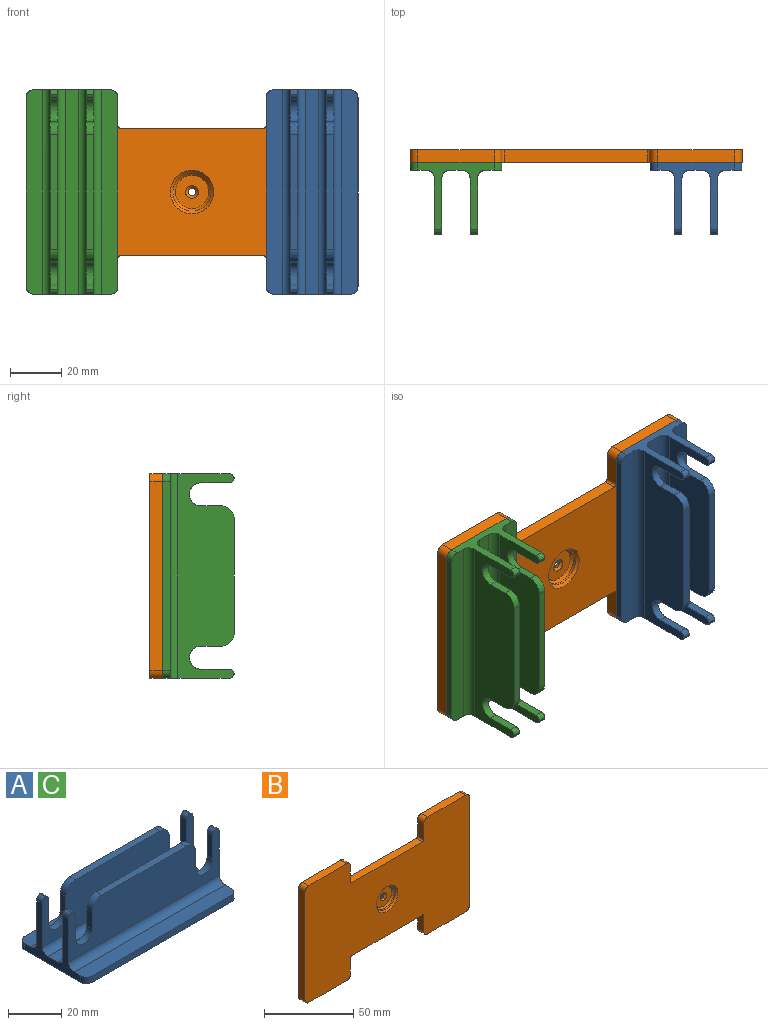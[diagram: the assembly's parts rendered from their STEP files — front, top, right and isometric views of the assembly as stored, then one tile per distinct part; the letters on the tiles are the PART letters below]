
ASSEMBLY  parts=3 mates=6
PART A: 151 faces, bbox 81.2x37.2x29.2 mm
  f0: plane 80x22mm, normal (0,1,0), area 1448.2mm2, adj f25,f26,f27,f116,f126,f128,f135,f136
  f1: plane 80x22mm, normal (0,-1,0), area 1448.2mm2, adj f25,f26,f27,f117,f126,f128,f135,f136
  f2: plane 81.23x23.23mm, normal (0,1,0), area 1448.2mm2, adj f124,f125,f126,f128,f129,f130,f131,f132
  f3: plane 80x22mm, normal (0,-1,0), area 1448.2mm2, adj f125,f126,f127,f128,f129,f130,f131,f132
  f4: plane 7.07x7.07mm, normal (0,0,-1), area 25mm2, adj f29,f30,f31,f32
  f5: plane 7.07x7.07mm, normal (0,0,-1), area 25mm2, adj f33,f34,f35,f36
  f6: plane 7.07x7.07mm, normal (0,0,-1), area 25mm2, adj f37,f38,f39,f40
  f7: plane 7.07x7.07mm, normal (0,0,-1), area 25mm2, adj f41,f42,f43,f44
  f8: plane 7.07x7.07mm, normal (0,0,-1), area 25mm2, adj f45,f46,f47,f48
  f9: plane 7.07x7.07mm, normal (0,0,-1), area 25mm2, adj f49,f50,f51,f52
  f10: plane 7.07x7.07mm, normal (0,0,-1), area 25mm2, adj f53,f54,f55,f56
  f11: plane 7.07x7.07mm, normal (0,0,-1), area 25mm2, adj f57,f58,f59,f60
  f12: plane 7.07x7.07mm, normal (0,0,-1), area 25mm2, adj f61,f62,f63,f64
  f13: plane 7.07x7.07mm, normal (0,0,-1), area 25mm2, adj f65,f66,f67,f68
  f14: plane 7.07x7.07mm, normal (0,0,-1), area 25mm2, adj f69,f70,f71,f72
  f15: plane 7.07x7.07mm, normal (0,0,-1), area 25mm2, adj f73,f74,f75,f76
  f16: plane 7.07x7.07mm, normal (0,0,-1), area 25mm2, adj f77,f78,f79,f80
  f17: plane 7.07x7.07mm, normal (0,0,-1), area 25mm2, adj f81,f82,f83,f84
  f18: plane 7.07x7.07mm, normal (0,0,-1), area 25mm2, adj f85,f86,f87,f88
  f19: plane 7.07x7.07mm, normal (0,0,-1), area 25mm2, adj f89,f90,f91,f92
  f20: plane 7.07x7.07mm, normal (0,0,-1), area 25mm2, adj f93,f94,f95,f96
  f21: plane 7.07x7.07mm, normal (0,0,-1), area 25mm2, adj f97,f98,f99,f100
  f22: plane 7.07x7.07mm, normal (0,0,-1), area 25mm2, adj f101,f102,f103,f104
  f23: plane 7.07x7.07mm, normal (0,0,-1), area 25mm2, adj f105,f106,f107,f108
  f24: plane 7.07x7.07mm, normal (0,0,-1), area 25mm2, adj f109,f110,f111,f112
  f25: plane 44.84x3mm, normal (0,0,1), area 134.5mm2, adj f0,f1,f141,f142
  f26: cylinder r=4.5mm len=9mm, axis (0,-1,0), area 42.4mm2, adj f0,f1,f135,f136
  f27: cylinder r=4.5mm len=9mm, axis (0,-1,0), area 42.4mm2, adj f0,f1,f137,f138
  f28: plane 74x3mm, normal (0,-1,0), area 222mm2, adj f114,f119,f120,f121
  f29: plane 3.54x3.54mm, normal (-0.71,-0.71,0), area 2.5mm2, adj f4,f30,f32,f121
  f30: plane 3.54x3.54mm, normal (0.71,-0.71,0), area 2.5mm2, adj f4,f29,f31,f121
  f31: plane 3.54x3.54mm, normal (0.71,0.71,0), area 2.5mm2, adj f4,f30,f32,f121
  f32: plane 3.54x3.54mm, normal (-0.71,0.71,0), area 2.5mm2, adj f4,f29,f31,f121
  f33: plane 3.54x3.54mm, normal (-0.71,-0.71,0), area 2.5mm2, adj f5,f34,f36,f121
  f34: plane 3.54x3.54mm, normal (0.71,-0.71,0), area 2.5mm2, adj f5,f33,f35,f121
  f35: plane 3.54x3.54mm, normal (0.71,0.71,0), area 2.5mm2, adj f5,f34,f36,f121
  f36: plane 3.54x3.54mm, normal (-0.71,0.71,0), area 2.5mm2, adj f5,f33,f35,f121
  f37: plane 3.54x3.54mm, normal (-0.71,-0.71,0), area 2.5mm2, adj f6,f38,f40,f121
  f38: plane 3.54x3.54mm, normal (0.71,-0.71,0), area 2.5mm2, adj f6,f37,f39,f121
  f39: plane 3.54x3.54mm, normal (0.71,0.71,0), area 2.5mm2, adj f6,f38,f40,f121
  f40: plane 3.54x3.54mm, normal (-0.71,0.71,0), area 2.5mm2, adj f6,f37,f39,f121
  f41: plane 3.54x3.54mm, normal (-0.71,-0.71,0), area 2.5mm2, adj f7,f42,f44,f121
  f42: plane 3.54x3.54mm, normal (0.71,-0.71,0), area 2.5mm2, adj f7,f41,f43,f121
  f43: plane 3.54x3.54mm, normal (0.71,0.71,0), area 2.5mm2, adj f7,f42,f44,f121
  f44: plane 3.54x3.54mm, normal (-0.71,0.71,0), area 2.5mm2, adj f7,f41,f43,f121
  f45: plane 3.54x3.54mm, normal (-0.71,-0.71,0), area 2.5mm2, adj f8,f46,f48,f121
  f46: plane 3.54x3.54mm, normal (0.71,-0.71,0), area 2.5mm2, adj f8,f45,f47,f121
  f47: plane 3.54x3.54mm, normal (0.71,0.71,0), area 2.5mm2, adj f8,f46,f48,f121
  f48: plane 3.54x3.54mm, normal (-0.71,0.71,0), area 2.5mm2, adj f8,f45,f47,f121
  f49: plane 3.54x3.54mm, normal (-0.71,-0.71,0), area 2.5mm2, adj f9,f50,f52,f121
  f50: plane 3.54x3.54mm, normal (0.71,-0.71,0), area 2.5mm2, adj f9,f49,f51,f121
  f51: plane 3.54x3.54mm, normal (0.71,0.71,0), area 2.5mm2, adj f9,f50,f52,f121
  f52: plane 3.54x3.54mm, normal (-0.71,0.71,0), area 2.5mm2, adj f9,f49,f51,f121
  f53: plane 3.54x3.54mm, normal (-0.71,-0.71,0), area 2.5mm2, adj f10,f54,f56,f121
  f54: plane 3.54x3.54mm, normal (0.71,-0.71,0), area 2.5mm2, adj f10,f53,f55,f121
  f55: plane 3.54x3.54mm, normal (0.71,0.71,0), area 2.5mm2, adj f10,f54,f56,f121
  f56: plane 3.54x3.54mm, normal (-0.71,0.71,0), area 2.5mm2, adj f10,f53,f55,f121
  f57: plane 3.54x3.54mm, normal (-0.71,-0.71,0), area 2.5mm2, adj f11,f58,f60,f121
  f58: plane 3.54x3.54mm, normal (0.71,-0.71,0), area 2.5mm2, adj f11,f57,f59,f121
  f59: plane 3.54x3.54mm, normal (0.71,0.71,0), area 2.5mm2, adj f11,f58,f60,f121
  f60: plane 3.54x3.54mm, normal (-0.71,0.71,0), area 2.5mm2, adj f11,f57,f59,f121
  f61: plane 3.54x3.54mm, normal (-0.71,-0.71,0), area 2.5mm2, adj f12,f62,f64,f121
  f62: plane 3.54x3.54mm, normal (0.71,-0.71,0), area 2.5mm2, adj f12,f61,f63,f121
  f63: plane 3.54x3.54mm, normal (0.71,0.71,0), area 2.5mm2, adj f12,f62,f64,f121
  f64: plane 3.54x3.54mm, normal (-0.71,0.71,0), area 2.5mm2, adj f12,f61,f63,f121
  f65: plane 3.54x3.54mm, normal (0.71,-0.71,0), area 2.5mm2, adj f13,f66,f68,f121
  f66: plane 3.54x3.54mm, normal (0.71,0.71,0), area 2.5mm2, adj f13,f65,f67,f121
  f67: plane 3.54x3.54mm, normal (-0.71,0.71,0), area 2.5mm2, adj f13,f66,f68,f121
  f68: plane 3.54x3.54mm, normal (-0.71,-0.71,0), area 2.5mm2, adj f13,f65,f67,f121
  f69: plane 3.54x3.54mm, normal (0.71,-0.71,0), area 2.5mm2, adj f14,f70,f72,f121
  f70: plane 3.54x3.54mm, normal (0.71,0.71,0), area 2.5mm2, adj f14,f69,f71,f121
  f71: plane 3.54x3.54mm, normal (-0.71,0.71,0), area 2.5mm2, adj f14,f70,f72,f121
  f72: plane 3.54x3.54mm, normal (-0.71,-0.71,0), area 2.5mm2, adj f14,f69,f71,f121
  f73: plane 3.54x3.54mm, normal (0.71,-0.71,0), area 2.5mm2, adj f15,f74,f76,f121
  f74: plane 3.54x3.54mm, normal (0.71,0.71,0), area 2.5mm2, adj f15,f73,f75,f121
  f75: plane 3.54x3.54mm, normal (-0.71,0.71,0), area 2.5mm2, adj f15,f74,f76,f121
  f76: plane 3.54x3.54mm, normal (-0.71,-0.71,0), area 2.5mm2, adj f15,f73,f75,f121
  f77: plane 3.54x3.54mm, normal (0.71,-0.71,0), area 2.5mm2, adj f16,f78,f80,f121
  f78: plane 3.54x3.54mm, normal (0.71,0.71,0), area 2.5mm2, adj f16,f77,f79,f121
  f79: plane 3.54x3.54mm, normal (-0.71,0.71,0), area 2.5mm2, adj f16,f78,f80,f121
  f80: plane 3.54x3.54mm, normal (-0.71,-0.71,0), area 2.5mm2, adj f16,f77,f79,f121
  f81: plane 3.54x3.54mm, normal (0.71,-0.71,0), area 2.5mm2, adj f17,f82,f84,f121
  f82: plane 3.54x3.54mm, normal (0.71,0.71,0), area 2.5mm2, adj f17,f81,f83,f121
  f83: plane 3.54x3.54mm, normal (-0.71,0.71,0), area 2.5mm2, adj f17,f82,f84,f121
  f84: plane 3.54x3.54mm, normal (-0.71,-0.71,0), area 2.5mm2, adj f17,f81,f83,f121
  f85: plane 3.54x3.54mm, normal (-0.71,-0.71,0), area 2.5mm2, adj f18,f86,f88,f121
  f86: plane 3.54x3.54mm, normal (0.71,-0.71,0), area 2.5mm2, adj f18,f85,f87,f121
  f87: plane 3.54x3.54mm, normal (0.71,0.71,0), area 2.5mm2, adj f18,f86,f88,f121
  f88: plane 3.54x3.54mm, normal (-0.71,0.71,0), area 2.5mm2, adj f18,f85,f87,f121
  f89: plane 3.54x3.54mm, normal (-0.71,-0.71,0), area 2.5mm2, adj f19,f90,f92,f121
  f90: plane 3.54x3.54mm, normal (0.71,-0.71,0), area 2.5mm2, adj f19,f89,f91,f121
  f91: plane 3.54x3.54mm, normal (0.71,0.71,0), area 2.5mm2, adj f19,f90,f92,f121
  f92: plane 3.54x3.54mm, normal (-0.71,0.71,0), area 2.5mm2, adj f19,f89,f91,f121
  f93: plane 3.54x3.54mm, normal (-0.71,-0.71,0), area 2.5mm2, adj f20,f94,f96,f121
  f94: plane 3.54x3.54mm, normal (0.71,-0.71,0), area 2.5mm2, adj f20,f93,f95,f121
  f95: plane 3.54x3.54mm, normal (0.71,0.71,0), area 2.5mm2, adj f20,f94,f96,f121
  f96: plane 3.54x3.54mm, normal (-0.71,0.71,0), area 2.5mm2, adj f20,f93,f95,f121
  f97: plane 3.54x3.54mm, normal (-0.71,-0.71,0), area 2.5mm2, adj f21,f98,f100,f121
  f98: plane 3.54x3.54mm, normal (0.71,-0.71,0), area 2.5mm2, adj f21,f97,f99,f121
  f99: plane 3.54x3.54mm, normal (0.71,0.71,0), area 2.5mm2, adj f21,f98,f100,f121
  f100: plane 3.54x3.54mm, normal (-0.71,0.71,0), area 2.5mm2, adj f21,f97,f99,f121
  f101: plane 3.54x3.54mm, normal (-0.71,-0.71,0), area 2.5mm2, adj f22,f102,f104,f121
  f102: plane 3.54x3.54mm, normal (0.71,-0.71,0), area 2.5mm2, adj f22,f101,f103,f121
  f103: plane 3.54x3.54mm, normal (0.71,0.71,0), area 2.5mm2, adj f22,f102,f104,f121
  f104: plane 3.54x3.54mm, normal (-0.71,0.71,0), area 2.5mm2, adj f22,f101,f103,f121
  f105: plane 3.54x3.54mm, normal (-0.71,-0.71,0), area 2.5mm2, adj f23,f106,f108,f121
  f106: plane 3.54x3.54mm, normal (0.71,-0.71,0), area 2.5mm2, adj f23,f105,f107,f121
  f107: plane 3.54x3.54mm, normal (0.71,0.71,0), area 2.5mm2, adj f23,f106,f108,f121
  f108: plane 3.54x3.54mm, normal (-0.71,0.71,0), area 2.5mm2, adj f23,f105,f107,f121
  f109: plane 3.54x3.54mm, normal (-0.71,-0.71,0), area 2.5mm2, adj f24,f110,f112,f121
  f110: plane 3.54x3.54mm, normal (0.71,-0.71,0), area 2.5mm2, adj f24,f109,f111,f121
  f111: plane 3.54x3.54mm, normal (0.71,0.71,0), area 2.5mm2, adj f24,f110,f112,f121
  f112: plane 3.54x3.54mm, normal (-0.71,0.71,0), area 2.5mm2, adj f24,f109,f111,f121
  f113: plane 74x3mm, normal (0,1,0), area 222mm2, adj f115,f121,f122,f123
  f114: cylinder r=3mm len=3mm, axis (0,0,-1), area 14.1mm2, adj f28,f119,f121,f126
  f115: cylinder r=3mm len=3mm, axis (0,0,-1), area 14.1mm2, adj f113,f121,f123,f126
  f116: cylinder r=3mm len=80mm, axis (1,0,0), area 377mm2, adj f0,f123,f126,f128
  f117: cylinder r=3mm len=80mm, axis (-1,0,0), area 377mm2, adj f1,f118,f126,f128
  f118: plane 80x5mm, normal (0,0,1), area 400mm2, adj f117,f124,f126,f128
  f119: plane 80.09x6.59mm, normal (0,0,1), area 515.9mm2, adj f28,f114,f120,f126,f127,f128
  f120: cylinder r=3mm len=3mm, axis (0,0,-1), area 14.1mm2, adj f28,f119,f121,f128
  f121: plane 80.09x36.09mm, normal (0,0,-1), area 2347mm2, adj f28,f29,f30,f31,f32,f33,f34,f35
  f122: cylinder r=3mm len=3mm, axis (0,0,-1), area 14.1mm2, adj f113,f121,f123,f128
  f123: plane 80x6.5mm, normal (0,0,1), area 516.1mm2, adj f113,f115,f116,f122,f126,f128
  f124: cylinder r=3mm len=80mm, axis (-1,0,0), area 377mm2, adj f2,f118,f126,f128
  f125: plane 44.84x3mm, normal (0,0,1), area 134.5mm2, adj f2,f3,f139,f140
  f126: plane 30.09x26.18mm, normal (1,0,0), area 236.3mm2, adj f0,f1,f2,f3,f114,f115,f116,f117
  f127: cylinder r=3mm len=80mm, axis (1,0,0), area 377mm2, adj f3,f119,f126,f128
  f128: plane 30x26.1mm, normal (-1,0,0), area 236.4mm2, adj f0,f1,f2,f3,f116,f117,f118,f119
  f129: cylinder r=4.5mm len=9mm, axis (0,1,0), area 42.4mm2, adj f2,f3,f131,f132
  f130: cylinder r=4.5mm len=9mm, axis (0,1,0), area 42.4mm2, adj f2,f3,f133,f134
  f131: plane 11.1x3mm, normal (1,0,0), area 33.3mm2, adj f2,f3,f129,f150
  f132: plane 7.92x3mm, normal (-1,0,0), area 23.8mm2, adj f2,f3,f129,f140
  f133: plane 11.1x3mm, normal (-1,0,0), area 33.3mm2, adj f2,f3,f130,f147
  f134: plane 7.92x3mm, normal (1,0,0), area 23.8mm2, adj f2,f3,f130,f139
  f135: plane 11.1x3mm, normal (1,0,0), area 33.3mm2, adj f0,f1,f26,f143
  f136: plane 7.92x3mm, normal (-1,0,0), area 23.8mm2, adj f0,f1,f26,f141
  f137: plane 11.1x3mm, normal (-1,0,0), area 33.3mm2, adj f0,f1,f27,f146
  f138: plane 7.92x3mm, normal (1,0,0), area 23.8mm2, adj f0,f1,f27,f142
  f139: cylinder r=5.08mm len=5.08mm, axis (0,-1,0), area 23.9mm2, adj f2,f3,f125,f134
  f140: cylinder r=5.08mm len=5.08mm, axis (0,1,0), area 23.9mm2, adj f2,f3,f125,f132
  f141: cylinder r=5.08mm len=5.08mm, axis (0,1,0), area 23.9mm2, adj f0,f1,f25,f136
  f142: cylinder r=5.08mm len=5.08mm, axis (0,-1,0), area 23.9mm2, adj f0,f1,f25,f138
  f143: cylinder r=1.91mm len=3mm, axis (0,1,0), area 8.5mm2, adj f0,f1,f135,f144
  f144: cylinder r=1.91mm len=3mm, axis (0,-1,0), area 8.5mm2, adj f0,f1,f128,f143
  f145: cylinder r=1.91mm len=3mm, axis (0,1,0), area 8.5mm2, adj f0,f1,f126,f146
  f146: cylinder r=1.91mm len=3mm, axis (0,1,0), area 8.5mm2, adj f0,f1,f137,f145
  f147: cylinder r=1.91mm len=3mm, axis (0,1,0), area 8.5mm2, adj f2,f3,f133,f148
  f148: cylinder r=1.91mm len=3mm, axis (0,1,0), area 8.5mm2, adj f2,f3,f126,f147
  f149: cylinder r=1.91mm len=3mm, axis (0,-1,0), area 8.5mm2, adj f2,f3,f128,f150
  f150: cylinder r=1.91mm len=3mm, axis (0,1,0), area 8.5mm2, adj f2,f3,f131,f149
PART B: 32 faces, bbox 130x5x80 mm
  f0: plane 30x5mm, normal (0,0,-1), area 150mm2, adj f2,f3,f15,f19
  f1: plane 30x5mm, normal (0,0,1), area 150mm2, adj f2,f3,f17,f20
  f2: plane 130x80mm, normal (0,-1,0), area 8418.4mm2, adj f0,f1,f4,f5,f6,f7,f8,f9
  f3: plane 130x80mm, normal (0,1,0), area 8638.3mm2, adj f0,f1,f4,f5,f6,f7,f8,f9
  f4: plane 74x5mm, normal (-1,0,0), area 370mm2, adj f2,f3,f18,f21
  f5: plane 30x5mm, normal (0,0,-1), area 150mm2, adj f2,f3,f14,f18
  f6: plane 74x5mm, normal (1,0,0), area 370mm2, adj f2,f3,f19,f20
  f7: plane 30x5mm, normal (0,0,1), area 150mm2, adj f2,f3,f16,f21
  f8: plane 11x5mm, normal (-1,0,0), area 55mm2, adj f2,f3,f15,f23
  f9: plane 56x5mm, normal (0,0,-1), area 280mm2, adj f2,f3,f23,f24
  f10: plane 11x5mm, normal (1,0,0), area 55mm2, adj f2,f3,f14,f24
  f11: plane 11x5mm, normal (1,0,0), area 55mm2, adj f2,f3,f16,f26
  f12: plane 56x5mm, normal (0,0,1), area 280mm2, adj f2,f3,f25,f26
  f13: plane 11x5mm, normal (-1,0,0), area 55mm2, adj f2,f3,f17,f25
  f14: cylinder r=3mm len=5mm, axis (0,-1,0), area 23.6mm2, adj f2,f3,f5,f10
  f15: cylinder r=3mm len=5mm, axis (0,1,0), area 23.6mm2, adj f0,f2,f3,f8
  f16: cylinder r=3mm len=5mm, axis (0,-1,0), area 23.6mm2, adj f2,f3,f7,f11
  f17: cylinder r=3mm len=5mm, axis (0,1,0), area 23.6mm2, adj f1,f2,f3,f13
  f18: cylinder r=3mm len=5mm, axis (0,1,0), area 23.6mm2, adj f2,f3,f4,f5
  f19: cylinder r=3mm len=5mm, axis (0,-1,0), area 23.6mm2, adj f0,f2,f3,f6
  f20: cylinder r=3mm len=5mm, axis (0,1,0), area 23.6mm2, adj f1,f2,f3,f6
  f21: cylinder r=3mm len=5mm, axis (0,-1,0), area 23.6mm2, adj f2,f3,f4,f7
  f22: cylinder r=1.5mm len=3mm, axis (0,-1,0), area 9.4mm2, adj f3,f29
  f23: cylinder r=1mm len=5mm, axis (0,-1,0), area 7.9mm2, adj f2,f3,f8,f9
  f24: cylinder r=1mm len=5mm, axis (0,1,0), area 7.9mm2, adj f2,f3,f9,f10
  f25: cylinder r=1mm len=5mm, axis (0,-1,0), area 7.9mm2, adj f2,f3,f12,f13
  f26: cylinder r=1mm len=5mm, axis (0,1,0), area 7.9mm2, adj f2,f3,f11,f12
  f27: cylinder r=7.5mm len=15mm, axis (0,-1,0), area 47.1mm2, adj f30,f31
  f28: plane 13x13mm, normal (0,-1,0), area 113.1mm2, adj f29,f30
  f29: cone r=1.5mm half-angle=45deg, axis (0,-1,0), area 17.8mm2, adj f22,f28
  f30: cone r=6.5mm half-angle=45deg, axis (0,-1,0), area 62.2mm2, adj f27,f28
  f31: cone r=7.5mm half-angle=45deg, axis (0,-1,0), area 71.1mm2, adj f2,f27
PART C: same geometry as A
PLACE A rot(axis=(0.58,0.58,-0.58),120deg) t=(38.04,16.2,28.24)mm
PLACE B t=(6.3,21.2,15.59)mm fixed
PLACE C rot(axis=(0.58,0.58,-0.58),120deg) t=(-55.96,16.2,28.24)mm
MATE planar C.f119 <-> A.f123  axis (0,-1,0) through (-70.69,13.2,28.24)mm
MATE planar A.f113 <-> B.f6  axis (1,0,0) through (56.04,16.2,28.24)mm
MATE planar A.f121 <-> B.f22  axis (0,-1,0) through (47.28,16.2,7.94)mm
MATE planar C.f28 <-> B.f4  axis (-1,0,0) through (-73.96,16.2,28.24)mm
MATE planar A.f128 <-> B.f1  axis (0,0,1) through (38.04,16.2,68.24)mm
MATE planar C.f128 <-> A.f128  axis (0,0,1) through (-55.96,16.2,68.24)mm
